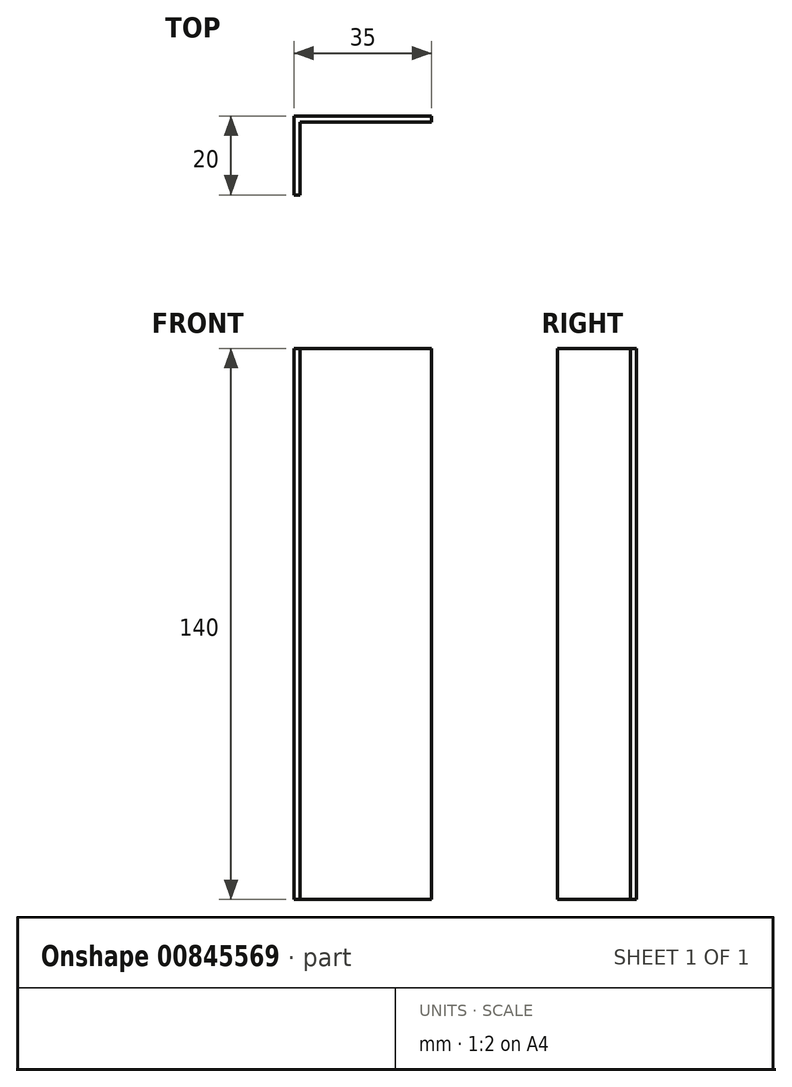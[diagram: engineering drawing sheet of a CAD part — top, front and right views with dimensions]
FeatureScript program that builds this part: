
annotation { "Feature Type Name" : "Feature", "Feature Type Description" : "" }
export const myFeature = defineFeature(function(context is Context, id is Id, definition is map)
    precondition{}
    {
        {
            var Q0;
            Q0=qCreatedBy(makeId("Top.planeOp"),FACE);
            var sketch = newSketch(context, id + "F0", { "sketchPlane" : qUnion([Q0])});
            skLineSegment(sketch, "E0", {"start": v(-34.92, 8.76) * mm, "end": v(-34.92, 28.76) * mm});
            skLineSegment(sketch, "E1", {"start": v(-34.92, 28.76) * mm, "end": v(0.08, 28.76) * mm});
            skLineSegment(sketch, "E2", {"start": v(0.08, 28.76) * mm, "end": v(0.08, 27.26) * mm});
            skLineSegment(sketch, "E3", {"start": v(0.08, 27.26) * mm, "end": v(-33.42, 27.26) * mm});
            skLineSegment(sketch, "E4", {"start": v(-33.42, 27.26) * mm, "end": v(-33.42, 8.76) * mm});
            skLineSegment(sketch, "E5", {"start": v(-33.42, 8.76) * mm, "end": v(-34.92, 8.76) * mm});
            skSolve(sketch);
        }
        {
            var Q0;
            Q0=makeQuery(id+"F0.imprint","IMPRINT",FACE,{"disambiguationData":[TD([[makeQuery(id+"F0.imprint","IMPRINT",EDGE,{"derivedFrom":sQuery(id+"F0.wireOp",EDGE,"E0")}),-1.0]])]});
            extrude(context, id + "F1", {"entities" : qUnion([Q0]), "depth" : 140 * mm, "offsetDistance" : 25 * mm});
        }
    });
